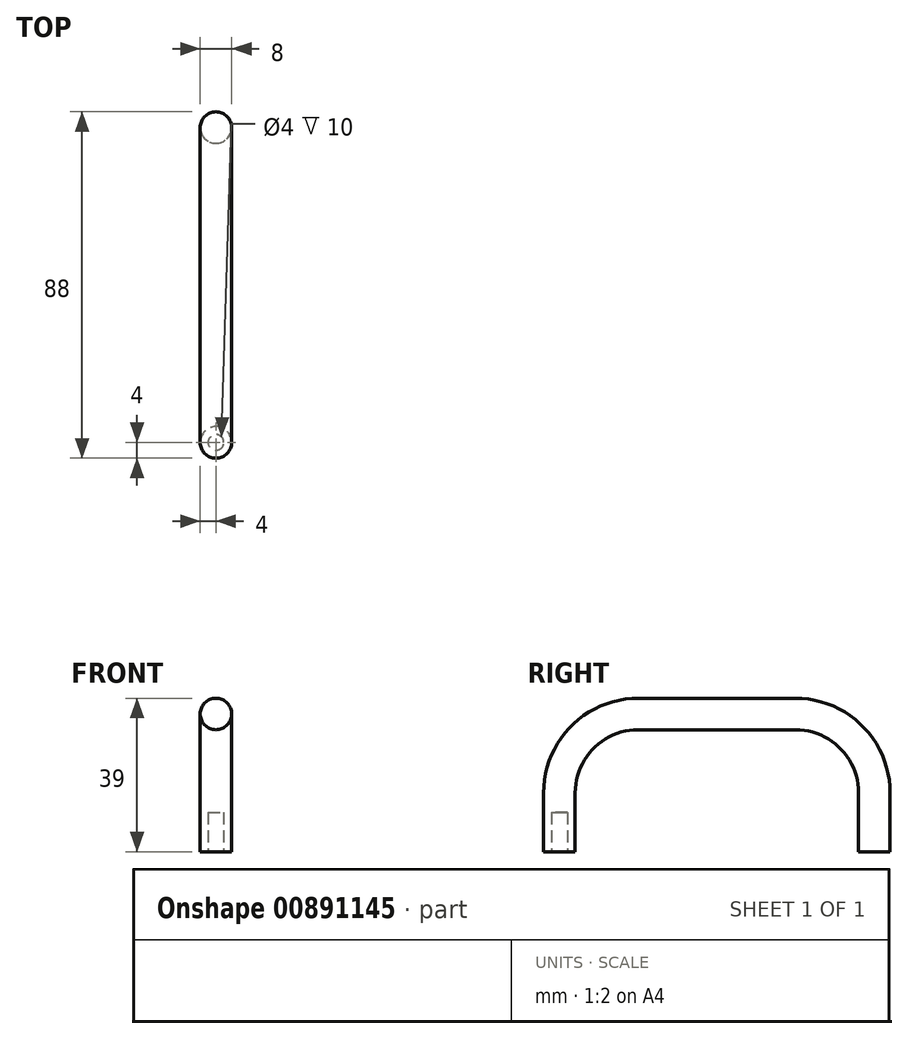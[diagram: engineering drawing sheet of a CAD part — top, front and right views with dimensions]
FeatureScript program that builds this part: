
annotation { "Feature Type Name" : "Feature", "Feature Type Description" : "" }
export const myFeature = defineFeature(function(context is Context, id is Id, definition is map)
    precondition{}
    {
        {
            var Q0;
            Q0=qCreatedBy(makeId("Right.planeOp"),FACE);
            var sketch = newSketch(context, id + "F0", { "sketchPlane" : qUnion([Q0])});
            skLineSegment(sketch, "E0", {"start": v(0, 0) * mm, "end": v(0, 15) * mm});
            skLineSegment(sketch, "E1", {"start": v(60, 35) * mm, "end": v(20, 35) * mm});
            skLineSegment(sketch, "E2", {"start": v(80, 15) * mm, "end": v(80, 0) * mm});
            skPoint(sketch, "E3.visualSharp", {"position": v(0, 35) * mm});
            skArc(sketch, "E3.filletArc", {"start": v(20, 35) * mm, "mid": v(5.86, 29.14) * mm, "end": v(0, 15) * mm});
            skPoint(sketch, "E4.visualSharp", {"position": v(80, 35) * mm});
            skArc(sketch, "E4.filletArc", {"start": v(80, 15) * mm, "mid": v(74.14, 29.14) * mm, "end": v(60, 35) * mm});
            skSolve(sketch);
        }
        {
            var Q0;
            Q0=qCreatedBy(makeId("Top.planeOp"),FACE);
            var sketch = newSketch(context, id + "F1", { "sketchPlane" : qUnion([Q0])});
            skCircle(sketch, "E5", {"center": v(0, 0) * mm, "radius": 4 * mm});
            skSolve(sketch);
        }
        {
            var Q0;
            Q0=makeQuery(id+"F1.imprint","IMPRINT",FACE,{"disambiguationData":[TD([[makeQuery(id+"F1.imprint","IMPRINT",EDGE,{"derivedFrom":sQuery(id+"F1.wireOp",EDGE,"E5")}),1.0]])]});
            var Q1;
            Q1=sQuery(id+"F0.wireOp",EDGE,"E0");
            var Q2;
            Q2=sQuery(id+"F0.wireOp",EDGE,"E3.filletArc");
            var Q3;
            Q3=sQuery(id+"F0.wireOp",EDGE,"E1");
            var Q4;
            Q4=sQuery(id+"F0.wireOp",EDGE,"E4.filletArc");
            var Q5;
            Q5=sQuery(id+"F0.wireOp",EDGE,"E2");
            sweep(context, id + "F2", {"profiles" : qUnion([Q0]), "path" : qUnion([Q1, Q2, Q3, Q4, Q5])});
        }
        {
            var Q0;
            Q0=makeQuery(id+"F2.opSweep","CAP_FACE",FACE,{"disambiguationData":[OSD([sQuery(id+"F0.wireOp",VERTEX,"E0.start"),sQuery(id+"F1.wireOp",EDGE,"E5")])],"isStart":true});
            var sketch = newSketch(context, id + "F3", { "sketchPlane" : qUnion([Q0])});
            skCircle(sketch, "E6", {"center": v(0, 0) * mm, "radius": 2 * mm});
            skLineSegment(sketch, "E7", {"start": v(-31.33, -50) * mm, "end": v(59.42, -50) * mm, "construction": true});
            skCircle(sketch, "E8.MirrorC", {"center": v(0, -100) * mm, "radius": 2 * mm});
            skSolve(sketch);
        }
        {
            var Q0;
            Q0 = qSketchRegion(id + "F3", true);
            extrude(context, id + "F4", {"entities" : qUnion([Q0]), "operationType" : NewBodyOperationType.REMOVE, "oppositeDirection" : true, "depth" : 10 * mm, "offsetDistance" : 25 * mm});
        }
    });
